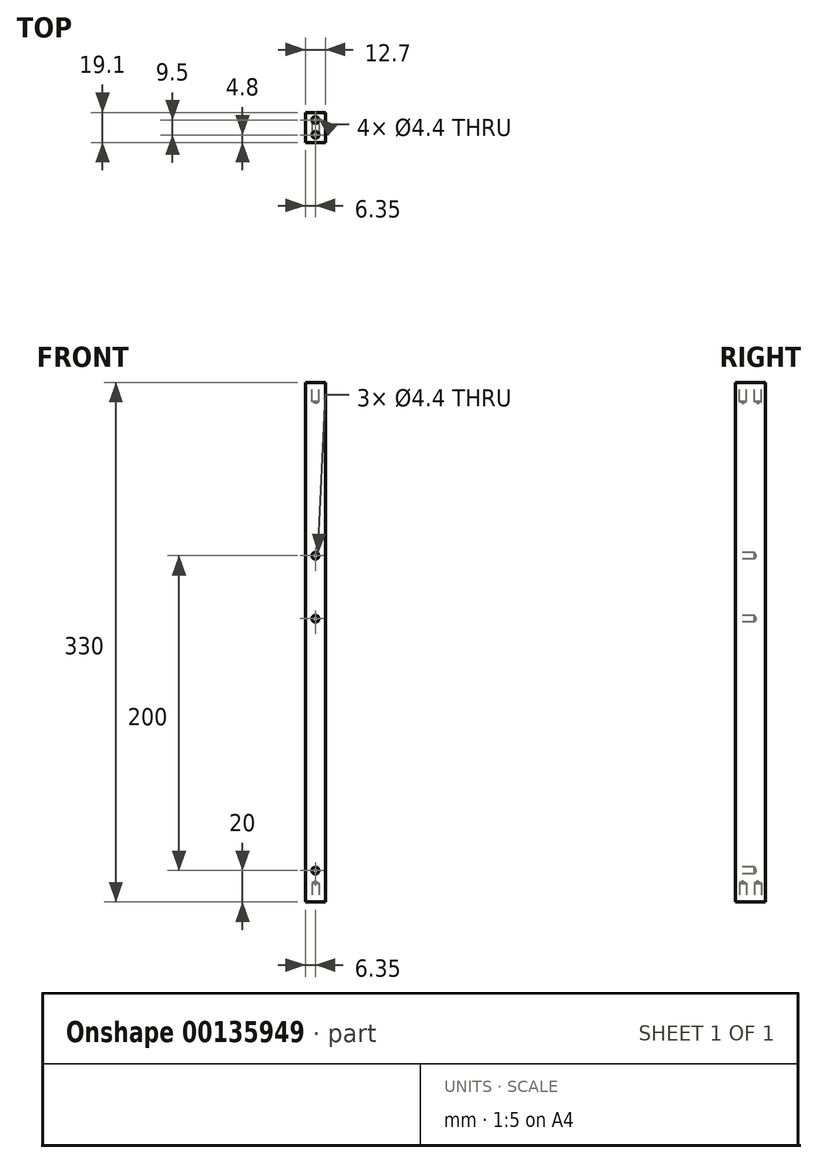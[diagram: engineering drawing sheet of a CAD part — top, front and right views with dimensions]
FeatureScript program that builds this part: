
annotation { "Feature Type Name" : "Feature", "Feature Type Description" : "" }
export const myFeature = defineFeature(function(context is Context, id is Id, definition is map)
    precondition{}
    {
        {
            var Q0;
            Q0=qCreatedBy(makeId("Front.planeOp"),FACE);
            var sketch = newSketch(context, id + "F0", { "sketchPlane" : qUnion([Q0])});
            skLineSegment(sketch, "E0.bottom", {"start": v(6.35, -165) * mm, "end": v(-6.35, -165) * mm});
            skLineSegment(sketch, "E0.top", {"start": v(6.35, 165) * mm, "end": v(-6.35, 165) * mm});
            skLineSegment(sketch, "E0.left", {"start": v(6.35, -165) * mm, "end": v(6.35, 165) * mm});
            skLineSegment(sketch, "E0.right", {"start": v(-6.35, -165) * mm, "end": v(-6.35, 165) * mm});
            skPoint(sketch, "E0.middle", {"position": v(0, 0) * mm});
            skSolve(sketch);
        }
        {
            var Q0;
            Q0 = qSketchRegion(id + "F0", true);
            extrude(context, id + "F1", {"entities" : qUnion([Q0]), "endBound" : BoundingType.SYMMETRIC, "depth" : 19.1 * mm});
        }
        {
            var Q0;
            Q0=makeQuery(id+"F1.opExtrude","CAP_FACE",FACE,{"disambiguationData":[OSD([sQuery(id+"F0.wireOp",EDGE,"E0.bottom"),sQuery(id+"F0.wireOp",EDGE,"E0.top"),sQuery(id+"F0.wireOp",EDGE,"E0.left"),sQuery(id+"F0.wireOp",EDGE,"E0.right")])],"isStart":false});
            var sketch = newSketch(context, id + "F2", { "sketchPlane" : qUnion([Q0])});
            skCircle(sketch, "E1", {"center": v(0, -145) * mm, "radius": 2 * mm});
            skCircle(sketch, "E2", {"center": v(0, 15) * mm, "radius": 2 * mm});
            skCircle(sketch, "E3", {"center": v(0, 55) * mm, "radius": 2 * mm});
            skSolve(sketch);
        }
        {
            var Q0;
            Q0=sQuery(id+"F2.wireOp",VERTEX,"E2.center");
            var Q1;
            Q1=sQuery(id+"F2.wireOp",VERTEX,"E1.center");
            var Q2;
            Q2=sQuery(id+"F2.wireOp",VERTEX,"E3.center");
            var Q3;
            Q3=sQuery(id+"F2.wireOp",VERTEX,"E3.center");
            var Q4;
            Q4=makeQuery(id+"F1.opExtrude","SWEPT_BODY",BODY,{"disambiguationData":[OSD([sQuery(id+"F0.wireOp",EDGE,"E0.bottom"),sQuery(id+"F0.wireOp",EDGE,"E0.top"),sQuery(id+"F0.wireOp",EDGE,"E0.left"),sQuery(id+"F0.wireOp",EDGE,"E0.right")])]});
            hole(context, id + "F3", {"style" : HoleStyle.SIMPLE, "endStyle" : HoleEndStyle.BLIND, "standardTappedOrClearance" : lookupTablePath({ "standard" : "ISO", "fit" : "Normal", "size" : "M4", "type" : "Clearance" }), "standardBlindInLast" : lookupTablePath({ "fit" : "Standard", "standard" : "ISO", "size" : "M4", "type" : "Clearance" }), "holeDiameter" : 4.4 * mm, "holeDepth" : 12 * mm, "locations" : qUnion([Q0, Q1, Q2, Q3]), "scope" : qUnion([Q4])});
        }
        {
            var Q0;
            Q0=makeQuery(id+"F1.opExtrude","SWEPT_FACE",FACE,{"disambiguationData":[OSD([sQuery(id+"F0.wireOp",EDGE,"E0.bottom")])]});
            var sketch = newSketch(context, id + "F4", { "sketchPlane" : qUnion([Q0])});
            skCircle(sketch, "E4", {"center": v(0, 4.75) * mm, "radius": 2 * mm});
            skCircle(sketch, "E5", {"center": v(0, -4.75) * mm, "radius": 2 * mm});
            skSolve(sketch);
        }
        {
            var Q0;
            Q0=makeQuery(id+"F1.opExtrude","SWEPT_FACE",FACE,{"disambiguationData":[OSD([sQuery(id+"F0.wireOp",EDGE,"E0.top")])]});
            var sketch = newSketch(context, id + "F5", { "sketchPlane" : qUnion([Q0])});
            skCircle(sketch, "E6", {"center": v(0, 4.75) * mm, "radius": 2 * mm});
            skCircle(sketch, "E7", {"center": v(0, -4.75) * mm, "radius": 2 * mm});
            skSolve(sketch);
        }
        {
            var Q0;
            Q0=sQuery(id+"F5.wireOp",VERTEX,"E6.center");
            var Q1;
            Q1=sQuery(id+"F5.wireOp",VERTEX,"E7.center");
            var Q2;
            Q2=sQuery(id+"F4.wireOp",VERTEX,"E4.center");
            var Q3;
            Q3=sQuery(id+"F4.wireOp",VERTEX,"E5.center");
            var Q4;
            Q4=makeQuery(id+"F1.opExtrude","SWEPT_BODY",BODY,{"disambiguationData":[OSD([sQuery(id+"F0.wireOp",EDGE,"E0.bottom"),sQuery(id+"F0.wireOp",EDGE,"E0.top"),sQuery(id+"F0.wireOp",EDGE,"E0.left"),sQuery(id+"F0.wireOp",EDGE,"E0.right")])]});
            hole(context, id + "F6", {"style" : HoleStyle.SIMPLE, "endStyle" : HoleEndStyle.BLIND, "standardTappedOrClearance" : lookupTablePath({ "standard" : "ISO", "fit" : "Normal", "size" : "M4", "type" : "Clearance" }), "standardBlindInLast" : lookupTablePath({ "fit" : "Standard", "standard" : "ISO", "size" : "M4", "type" : "Clearance" }), "holeDiameter" : 4.4 * mm, "holeDepth" : 12 * mm, "locations" : qUnion([Q0, Q1, Q2, Q3]), "scope" : qUnion([Q4])});
        }
    });
